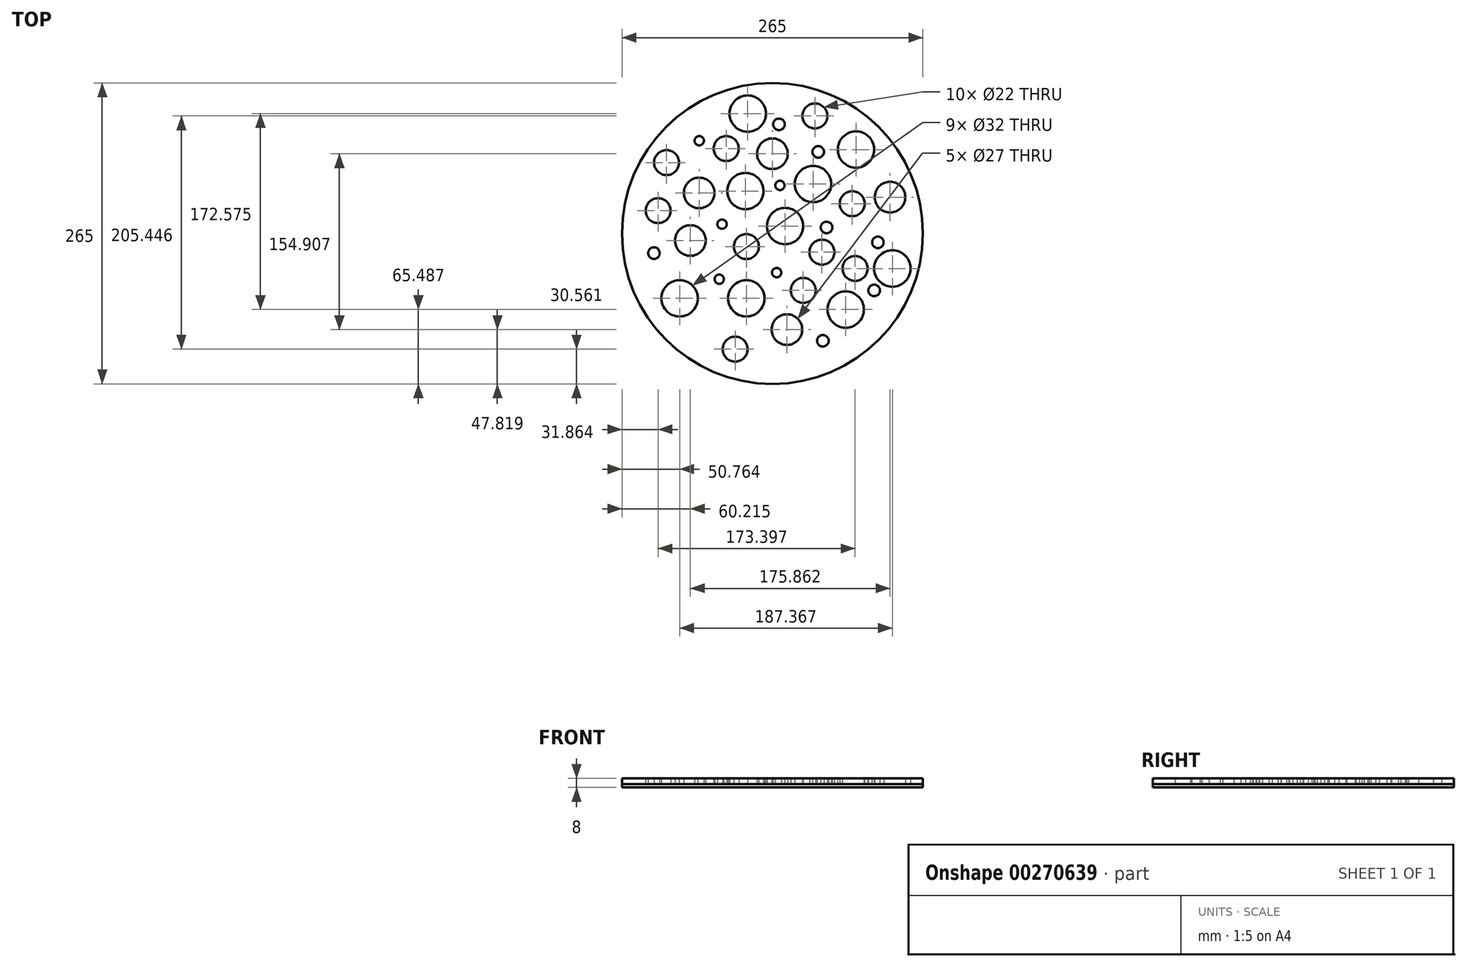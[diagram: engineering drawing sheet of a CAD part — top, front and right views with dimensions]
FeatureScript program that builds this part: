
annotation { "Feature Type Name" : "Feature", "Feature Type Description" : "" }
export const myFeature = defineFeature(function(context is Context, id is Id, definition is map)
    precondition{}
    {
        {
            var Q0;
            Q0=qCreatedBy(makeId("Top.planeOp"),FACE);
            var sketch = newSketch(context, id + "F0", { "sketchPlane" : qUnion([Q0])});
            skCircle(sketch, "E0", {"center": v(0, 0) * mm, "radius": 132.5 * mm});
            skCircle(sketch, "E1", {"center": v(27.15, -50.17) * mm, "radius": 11 * mm});
            skCircle(sketch, "E2", {"center": v(70.3, 26.26) * mm, "radius": 11 * mm});
            skCircle(sketch, "E3", {"center": v(-40.65, 74.75) * mm, "radius": 11 * mm});
            skCircle(sketch, "E4", {"center": v(-100.64, 20.1) * mm, "radius": 11 * mm});
            skCircle(sketch, "E5", {"center": v(-32.84, -101.94) * mm, "radius": 11 * mm});
            skCircle(sketch, "E6", {"center": v(37.42, 103.5) * mm, "radius": 11 * mm});
            skCircle(sketch, "E7", {"center": v(6.6, 42.28) * mm, "radius": 4.1 * mm});
            skCircle(sketch, "E8", {"center": v(-46.8, -40.3) * mm, "radius": 4.1 * mm});
            skCircle(sketch, "E9", {"center": v(3.73, -34.55) * mm, "radius": 4.1 * mm});
            skCircle(sketch, "E10", {"center": v(-44.34, 8.18) * mm, "radius": 4.1 * mm});
            skCircle(sketch, "E11", {"center": v(-64.48, 81.73) * mm, "radius": 4.1 * mm});
            skCircle(sketch, "E12", {"center": v(47.7, 5.3) * mm, "radius": 5.1 * mm});
            skCircle(sketch, "E13", {"center": v(44.4, -94.54) * mm, "radius": 5.1 * mm});
            skCircle(sketch, "E14", {"center": v(5.78, 96.11) * mm, "radius": 5.1 * mm});
            skCircle(sketch, "E15", {"center": v(-104.33, -17.3) * mm, "radius": 5.1 * mm});
            skCircle(sketch, "E16", {"center": v(40.3, 71.87) * mm, "radius": 5.1 * mm});
            skCircle(sketch, "E17", {"center": v(89.6, -50.17) * mm, "radius": 5.1 * mm});
            skCircle(sketch, "E18", {"center": v(92.9, -7.84) * mm, "radius": 5.1 * mm});
            skCircle(sketch, "E19", {"center": v(-22.98, -57.15) * mm, "radius": 16 * mm});
            skCircle(sketch, "E20", {"center": v(-23.8, 37.35) * mm, "radius": 16 * mm});
            skCircle(sketch, "E21", {"center": v(11.13, 6.54) * mm, "radius": 16 * mm});
            skCircle(sketch, "E22", {"center": v(64.54, -67.01) * mm, "radius": 16 * mm});
            skCircle(sketch, "E23", {"center": v(-81.74, -57.15) * mm, "radius": 16 * mm});
            skCircle(sketch, "E24", {"center": v(-21.75, 105.56) * mm, "radius": 16 * mm});
            skCircle(sketch, "E25", {"center": v(73.58, 73.92) * mm, "radius": 16 * mm});
            skCircle(sketch, "E26", {"center": v(35.78, 43.52) * mm, "radius": 16 * mm});
            skCircle(sketch, "E27", {"center": v(72.76, -30.85) * mm, "radius": 11 * mm});
            skCircle(sketch, "E28", {"center": v(43.59, -16.47) * mm, "radius": 11 * mm});
            skCircle(sketch, "E29", {"center": v(-93.24, 62.42) * mm, "radius": 11 * mm});
            skCircle(sketch, "E30", {"center": v(-22.98, -11.54) * mm, "radius": 11 * mm});
            skCircle(sketch, "E31", {"center": v(-64.48, 35.71) * mm, "radius": 13.5 * mm});
            skCircle(sketch, "E32", {"center": v(0, 70.23) * mm, "radius": 13.5 * mm});
            skCircle(sketch, "E33", {"center": v(103.58, 32.01) * mm, "radius": 13.5 * mm});
            skCircle(sketch, "E34", {"center": v(-72.28, -6.2) * mm, "radius": 13.5 * mm});
            skCircle(sketch, "E35", {"center": v(12.77, -84.68) * mm, "radius": 13.5 * mm});
            skCircle(sketch, "E36", {"center": v(105.63, -30.85) * mm, "radius": 16 * mm});
            skSolve(sketch);
        }
        {
            var Q0;
            Q0=makeQuery(id+"F0.imprint","IMPRINT",FACE,{"disambiguationData":[TD([[makeQuery(id+"F0.imprint","IMPRINT",EDGE,{"derivedFrom":sQuery(id+"F0.wireOp",EDGE,"E0")}),1.0]])]});
            extrude(context, id + "F1", {"entities" : qUnion([Q0]), "depth" : 5 * mm});
        }
        {
            var Q0;
            Q0=makeQuery(id+"F0.imprint","IMPRINT",FACE,{"disambiguationData":[TD([[makeQuery(id+"F0.imprint","IMPRINT",EDGE,{"derivedFrom":sQuery(id+"F0.wireOp",EDGE,"E0")}),1.0]])]});
            var Q1;
            Q1=makeQuery(id+"F0.imprint","IMPRINT",FACE,{"disambiguationData":[TD([[makeQuery(id+"F0.imprint","IMPRINT",EDGE,{"derivedFrom":sQuery(id+"F0.wireOp",EDGE,"E20")}),1.0]])]});
            var Q2;
            Q2=makeQuery(id+"F0.imprint","IMPRINT",FACE,{"disambiguationData":[TD([[makeQuery(id+"F0.imprint","IMPRINT",EDGE,{"derivedFrom":sQuery(id+"F0.wireOp",EDGE,"E36")}),1.0]])]});
            var Q3;
            Q3=makeQuery(id+"F0.imprint","IMPRINT",FACE,{"disambiguationData":[TD([[makeQuery(id+"F0.imprint","IMPRINT",EDGE,{"derivedFrom":sQuery(id+"F0.wireOp",EDGE,"E27")}),1.0]])]});
            var Q4;
            Q4=makeQuery(id+"F0.imprint","IMPRINT",FACE,{"disambiguationData":[TD([[makeQuery(id+"F0.imprint","IMPRINT",EDGE,{"derivedFrom":sQuery(id+"F0.wireOp",EDGE,"E23")}),1.0]])]});
            var Q5;
            Q5=makeQuery(id+"F0.imprint","IMPRINT",FACE,{"disambiguationData":[TD([[makeQuery(id+"F0.imprint","IMPRINT",EDGE,{"derivedFrom":sQuery(id+"F0.wireOp",EDGE,"E21")}),1.0]])]});
            var Q6;
            Q6=makeQuery(id+"F0.imprint","IMPRINT",FACE,{"disambiguationData":[TD([[makeQuery(id+"F0.imprint","IMPRINT",EDGE,{"derivedFrom":sQuery(id+"F0.wireOp",EDGE,"E16")}),1.0]])]});
            var Q7;
            Q7=makeQuery(id+"F0.imprint","IMPRINT",FACE,{"disambiguationData":[TD([[makeQuery(id+"F0.imprint","IMPRINT",EDGE,{"derivedFrom":sQuery(id+"F0.wireOp",EDGE,"E30")}),1.0]])]});
            var Q8;
            Q8=makeQuery(id+"F0.imprint","IMPRINT",FACE,{"disambiguationData":[TD([[makeQuery(id+"F0.imprint","IMPRINT",EDGE,{"derivedFrom":sQuery(id+"F0.wireOp",EDGE,"E14")}),1.0]])]});
            var Q9;
            Q9=makeQuery(id+"F0.imprint","IMPRINT",FACE,{"disambiguationData":[TD([[makeQuery(id+"F0.imprint","IMPRINT",EDGE,{"derivedFrom":sQuery(id+"F0.wireOp",EDGE,"E15")}),1.0]])]});
            var Q10;
            Q10=makeQuery(id+"F0.imprint","IMPRINT",FACE,{"disambiguationData":[TD([[makeQuery(id+"F0.imprint","IMPRINT",EDGE,{"derivedFrom":sQuery(id+"F0.wireOp",EDGE,"E17")}),1.0]])]});
            var Q11;
            Q11=makeQuery(id+"F0.imprint","IMPRINT",FACE,{"disambiguationData":[TD([[makeQuery(id+"F0.imprint","IMPRINT",EDGE,{"derivedFrom":sQuery(id+"F0.wireOp",EDGE,"E33")}),1.0]])]});
            var Q12;
            Q12=makeQuery(id+"F0.imprint","IMPRINT",FACE,{"disambiguationData":[TD([[makeQuery(id+"F0.imprint","IMPRINT",EDGE,{"derivedFrom":sQuery(id+"F0.wireOp",EDGE,"E1")}),1.0]])]});
            var Q13;
            Q13=makeQuery(id+"F0.imprint","IMPRINT",FACE,{"disambiguationData":[TD([[makeQuery(id+"F0.imprint","IMPRINT",EDGE,{"derivedFrom":sQuery(id+"F0.wireOp",EDGE,"E2")}),1.0]])]});
            var Q14;
            Q14=makeQuery(id+"F0.imprint","IMPRINT",FACE,{"disambiguationData":[TD([[makeQuery(id+"F0.imprint","IMPRINT",EDGE,{"derivedFrom":sQuery(id+"F0.wireOp",EDGE,"E3")}),1.0]])]});
            var Q15;
            Q15=makeQuery(id+"F0.imprint","IMPRINT",FACE,{"disambiguationData":[TD([[makeQuery(id+"F0.imprint","IMPRINT",EDGE,{"derivedFrom":sQuery(id+"F0.wireOp",EDGE,"E4")}),1.0]])]});
            var Q16;
            Q16=makeQuery(id+"F0.imprint","IMPRINT",FACE,{"disambiguationData":[TD([[makeQuery(id+"F0.imprint","IMPRINT",EDGE,{"derivedFrom":sQuery(id+"F0.wireOp",EDGE,"E5")}),1.0]])]});
            var Q17;
            Q17=makeQuery(id+"F0.imprint","IMPRINT",FACE,{"disambiguationData":[TD([[makeQuery(id+"F0.imprint","IMPRINT",EDGE,{"derivedFrom":sQuery(id+"F0.wireOp",EDGE,"E6")}),1.0]])]});
            var Q18;
            Q18=makeQuery(id+"F0.imprint","IMPRINT",FACE,{"disambiguationData":[TD([[makeQuery(id+"F0.imprint","IMPRINT",EDGE,{"derivedFrom":sQuery(id+"F0.wireOp",EDGE,"E12")}),1.0]])]});
            var Q19;
            Q19=makeQuery(id+"F0.imprint","IMPRINT",FACE,{"disambiguationData":[TD([[makeQuery(id+"F0.imprint","IMPRINT",EDGE,{"derivedFrom":sQuery(id+"F0.wireOp",EDGE,"E13")}),1.0]])]});
            var Q20;
            Q20=makeQuery(id+"F0.imprint","IMPRINT",FACE,{"disambiguationData":[TD([[makeQuery(id+"F0.imprint","IMPRINT",EDGE,{"derivedFrom":sQuery(id+"F0.wireOp",EDGE,"E28")}),1.0]])]});
            var Q21;
            Q21=makeQuery(id+"F0.imprint","IMPRINT",FACE,{"disambiguationData":[TD([[makeQuery(id+"F0.imprint","IMPRINT",EDGE,{"derivedFrom":sQuery(id+"F0.wireOp",EDGE,"E22")}),1.0]])]});
            var Q22;
            Q22=makeQuery(id+"F0.imprint","IMPRINT",FACE,{"disambiguationData":[TD([[makeQuery(id+"F0.imprint","IMPRINT",EDGE,{"derivedFrom":sQuery(id+"F0.wireOp",EDGE,"E31")}),1.0]])]});
            var Q23;
            Q23=makeQuery(id+"F0.imprint","IMPRINT",FACE,{"disambiguationData":[TD([[makeQuery(id+"F0.imprint","IMPRINT",EDGE,{"derivedFrom":sQuery(id+"F0.wireOp",EDGE,"E18")}),1.0]])]});
            var Q24;
            Q24=makeQuery(id+"F0.imprint","IMPRINT",FACE,{"disambiguationData":[TD([[makeQuery(id+"F0.imprint","IMPRINT",EDGE,{"derivedFrom":sQuery(id+"F0.wireOp",EDGE,"E34")}),1.0]])]});
            var Q25;
            Q25=makeQuery(id+"F0.imprint","IMPRINT",FACE,{"disambiguationData":[TD([[makeQuery(id+"F0.imprint","IMPRINT",EDGE,{"derivedFrom":sQuery(id+"F0.wireOp",EDGE,"E29")}),1.0]])]});
            var Q26;
            Q26=makeQuery(id+"F0.imprint","IMPRINT",FACE,{"disambiguationData":[TD([[makeQuery(id+"F0.imprint","IMPRINT",EDGE,{"derivedFrom":sQuery(id+"F0.wireOp",EDGE,"E25")}),1.0]])]});
            var Q27;
            Q27=makeQuery(id+"F0.imprint","IMPRINT",FACE,{"disambiguationData":[TD([[makeQuery(id+"F0.imprint","IMPRINT",EDGE,{"derivedFrom":sQuery(id+"F0.wireOp",EDGE,"E19")}),1.0]])]});
            var Q28;
            Q28=makeQuery(id+"F0.imprint","IMPRINT",FACE,{"disambiguationData":[TD([[makeQuery(id+"F0.imprint","IMPRINT",EDGE,{"derivedFrom":sQuery(id+"F0.wireOp",EDGE,"E35")}),1.0]])]});
            var Q29;
            Q29=makeQuery(id+"F0.imprint","IMPRINT",FACE,{"disambiguationData":[TD([[makeQuery(id+"F0.imprint","IMPRINT",EDGE,{"derivedFrom":sQuery(id+"F0.wireOp",EDGE,"E32")}),1.0]])]});
            var Q30;
            Q30=makeQuery(id+"F0.imprint","IMPRINT",FACE,{"disambiguationData":[TD([[makeQuery(id+"F0.imprint","IMPRINT",EDGE,{"derivedFrom":sQuery(id+"F0.wireOp",EDGE,"E26")}),1.0]])]});
            var Q31;
            Q31=makeQuery(id+"F0.imprint","IMPRINT",FACE,{"disambiguationData":[TD([[makeQuery(id+"F0.imprint","IMPRINT",EDGE,{"derivedFrom":sQuery(id+"F0.wireOp",EDGE,"E7")}),1.0]])]});
            var Q32;
            Q32=makeQuery(id+"F0.imprint","IMPRINT",FACE,{"disambiguationData":[TD([[makeQuery(id+"F0.imprint","IMPRINT",EDGE,{"derivedFrom":sQuery(id+"F0.wireOp",EDGE,"E8")}),1.0]])]});
            var Q33;
            Q33=makeQuery(id+"F0.imprint","IMPRINT",FACE,{"disambiguationData":[TD([[makeQuery(id+"F0.imprint","IMPRINT",EDGE,{"derivedFrom":sQuery(id+"F0.wireOp",EDGE,"E9")}),1.0]])]});
            var Q34;
            Q34=makeQuery(id+"F0.imprint","IMPRINT",FACE,{"disambiguationData":[TD([[makeQuery(id+"F0.imprint","IMPRINT",EDGE,{"derivedFrom":sQuery(id+"F0.wireOp",EDGE,"E10")}),1.0]])]});
            var Q35;
            Q35=makeQuery(id+"F0.imprint","IMPRINT",FACE,{"disambiguationData":[TD([[makeQuery(id+"F0.imprint","IMPRINT",EDGE,{"derivedFrom":sQuery(id+"F0.wireOp",EDGE,"E11")}),1.0]])]});
            var Q36;
            Q36=makeQuery(id+"F0.imprint","IMPRINT",FACE,{"disambiguationData":[TD([[makeQuery(id+"F0.imprint","IMPRINT",EDGE,{"derivedFrom":sQuery(id+"F0.wireOp",EDGE,"E24")}),1.0]])]});
            extrude(context, id + "F2", {"entities" : qUnion([Q0, Q1, Q2, Q3, Q4, Q5, Q6, Q7, Q8, Q9, Q10, Q11, Q12, Q13, Q14, Q15, Q16, Q17, Q18, Q19, Q20, Q21, Q22, Q23, Q24, Q25, Q26, Q27, Q28, Q29, Q30, Q31, Q32, Q33, Q34, Q35, Q36]), "oppositeDirection" : true, "depth" : 3 * mm});
        }
    });
